# Revit family: Comfort_Window_A_Top_Hung_Standard
name_source: partatom
category: Windows
revit_build: Autodesk Revit 2014 (Build: 20130308_1515(x64)
units: mm (PartAtom-declared; Revit-internal decimal feet)

## types (2) — shared parameters
DG Gasket Thickness = 12 mm  [stored 0.0393701 ft]
Description = Comfort Window, Top Hung, Type A
Double Glazing Gasket Finish = Double Glazing Gasket Material
Frame Depth = 33 mm  [stored 0.108268 ft]
Limit Sash Height Max = 1200 mm
Limit Sash Height Min = 300 mm  [stored 0.984252 ft]
Limit Sash Width Max = 1200 mm
Limit Sash Width Min = 300 mm  [stored 0.984252 ft]
Limit Window Height Max = 1275 mm  [stored 4.18307 ft]
Limit Window Height Min = 375 mm  [stored 1.23031 ft]
Limit Window Width Max = 1275 mm  [stored 4.18307 ft]
Limit Window Width Min = 375 mm  [stored 1.23031 ft]
Manufacturer = Crealco
Max System DG One Piece Thickness = 4 mm  [stored 0.0131234 ft]
Max System DG Unit Thickness = 20 mm  [stored 0.0656168 ft]
Model = Comfort Window
Rough Height = 1647 mm
Rough Width = 2226 mm
Sash Frame Gap = 5 mm  [stored 0.0164042 ft]
Sash Side Gap = 38 mm
URL = http://www.crealco.co.za
Window Height = 590 mm  [stored 1.9357 ft]
zero-valued in all types: Visual Light Transmittance

## per-type parameters (varying)
| type | Clearvue SHGC Value | Clearvue U Value | Energy Advantage SHGC Value | Energy Advantage U Value | Intruderprufe LowE SHGC Value | Intruderprufe LowE U Value | Intruderprufe SHGC Value | Intruderprufe U Value | SmartGlass Elite SHGC Value | SmartGlass Elite U Value | SmartGlass Plus SHGC Value | SmartGlass Plus U Value | SmartGlass Standard SHGC Value | SmartGlass Standard U Value | SmartGlass Superior SHGC Value | SmartGlass Superior U Value | Window Width |
| Comfort-0606T | 0.481 | 6.14 | 0.433 | 5.04 | 0.412 | 4.92 | 0.459 | 6.05 | 0.242 | 3.98 | 0.325 | 4.09 | 0.432 | 4.5 | 0.213 | 3.98 | 590 mm  [stored 1.9357 ft] |
| Comfort-0906T | 0.534 | 6.1 | 0.479 | 4.85 | 0.454 | 4.74 | 0.508 | 6.01 | 0.265 | 3.66 | 0.357 | 3.79 | 0.477 | 4.25 | 0.232 | 3.67 | 890 mm  [stored 2.91995 ft] |

note: [stored X ft] marks values corroborated as IEEE doubles in the binary element streams (Revit-internal decimal feet)

## geometry (parser evidence)
native form markers: Sweep x12
no freeform markers — native parametric forms only
